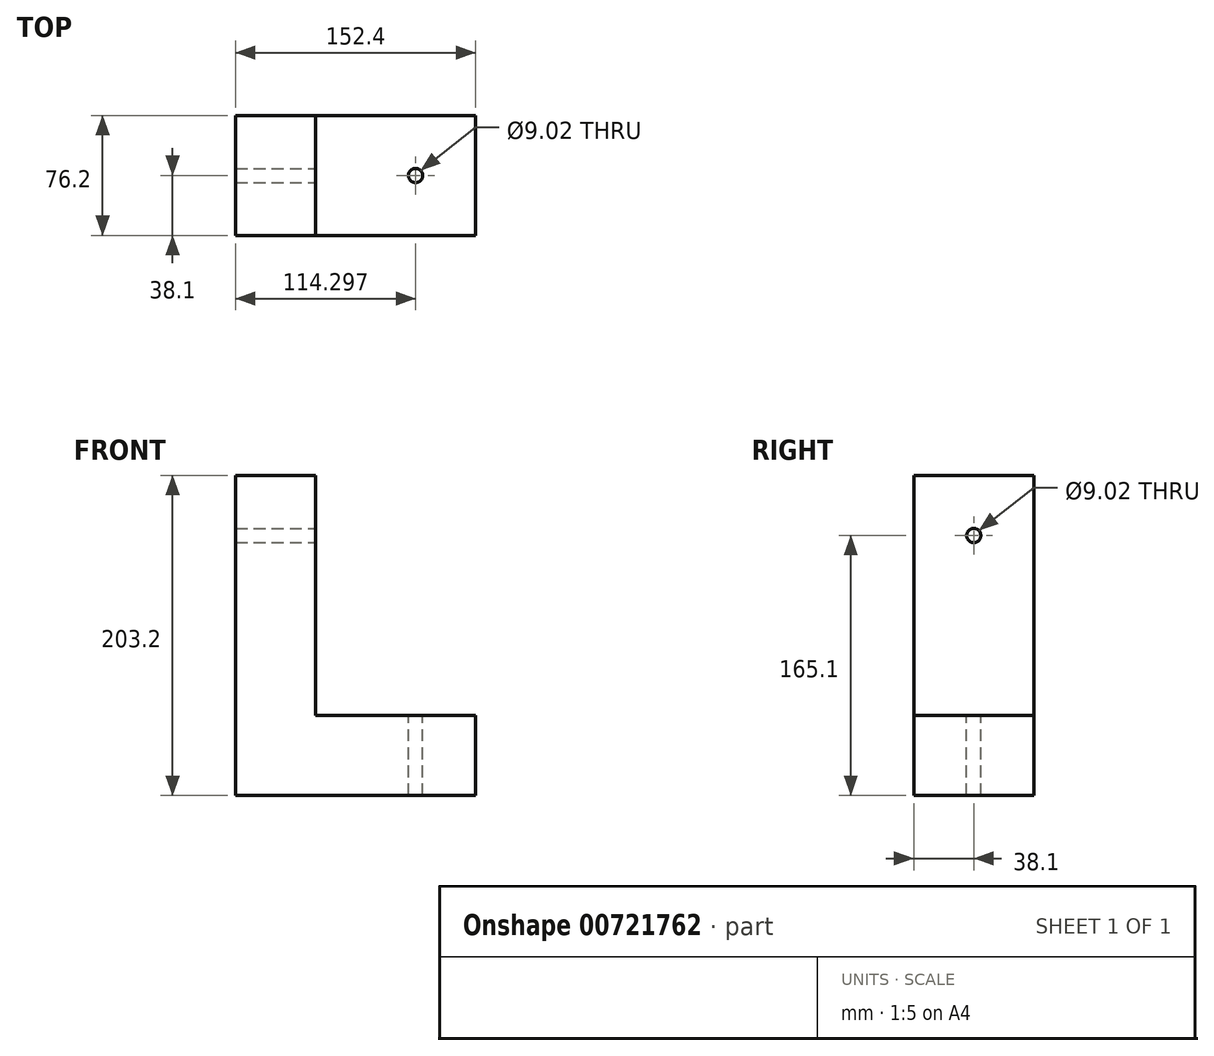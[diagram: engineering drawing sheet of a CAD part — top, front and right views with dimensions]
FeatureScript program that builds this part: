
annotation { "Feature Type Name" : "Feature", "Feature Type Description" : "" }
export const myFeature = defineFeature(function(context is Context, id is Id, definition is map)
    precondition{}
    {
        {
            var Q0;
            Q0=qCreatedBy(makeId("Front.planeOp"),FACE);
            var sketch = newSketch(context, id + "F0", { "sketchPlane" : qUnion([Q0])});
            skLineSegment(sketch, "E0", {"start": v(-120.04, 104.09) * mm, "end": v(-120.04, -99.11) * mm});
            skLineSegment(sketch, "E1", {"start": v(-120.04, -99.11) * mm, "end": v(32.36, -99.11) * mm});
            skLineSegment(sketch, "E2", {"start": v(32.36, -99.11) * mm, "end": v(32.36, -48.31) * mm});
            skLineSegment(sketch, "E3", {"start": v(32.36, -48.31) * mm, "end": v(-69.24, -48.31) * mm});
            skLineSegment(sketch, "E4", {"start": v(-69.24, -48.31) * mm, "end": v(-69.24, 104.09) * mm});
            skLineSegment(sketch, "E5", {"start": v(-69.24, 104.09) * mm, "end": v(-120.04, 104.09) * mm});
            skSolve(sketch);
        }
        {
            var Q0;
            Q0 = qSketchRegion(id + "F0", true);
            extrude(context, id + "F1", {"entities" : qUnion([Q0]), "depth" : 76.2 * mm, "offsetDistance" : 25.4 * mm});
        }
        {
            var Q0;
            Q0=makeQuery(id+"F1.opExtrude","SWEPT_FACE",FACE,{"disambiguationData":[OSD([sQuery(id+"F0.wireOp",EDGE,"E4")])]});
            var sketch = newSketch(context, id + "F2", { "sketchPlane" : qUnion([Q0])});
            skCircle(sketch, "E6", {"center": v(-38.1, 65.99) * mm, "radius": 4.5 * mm});
            skSolve(sketch);
        }
        {
            var Q0;
            Q0=qCreatedBy(makeId("Top.planeOp"),FACE);
            var sketch = newSketch(context, id + "F3", { "sketchPlane" : qUnion([Q0])});
            skCircle(sketch, "E7", {"center": v(-5.74, -38.1) * mm, "radius": 4.5 * mm});
            skSolve(sketch);
        }
        {
            var Q0;
            Q0 = qSketchRegion(id + "F3", true);
            extrude(context, id + "F4", {"entities" : qUnion([Q0]), "operationType" : NewBodyOperationType.REMOVE, "oppositeDirection" : true, "depth" : 101.6 * mm, "offsetDistance" : 25.4 * mm});
        }
        {
            var Q0;
            Q0=makeQuery(id+"F2.imprint","IMPRINT",FACE,{"disambiguationData":[TD([[makeQuery(id+"F2.imprint","IMPRINT",EDGE,{"derivedFrom":sQuery(id+"F2.wireOp",EDGE,"E6")}),1.0]])]});
            extrude(context, id + "F5", {"entities" : qUnion([Q0]), "operationType" : NewBodyOperationType.REMOVE, "oppositeDirection" : true, "depth" : 584.2 * mm, "offsetDistance" : 25.4 * mm});
        }
    });
